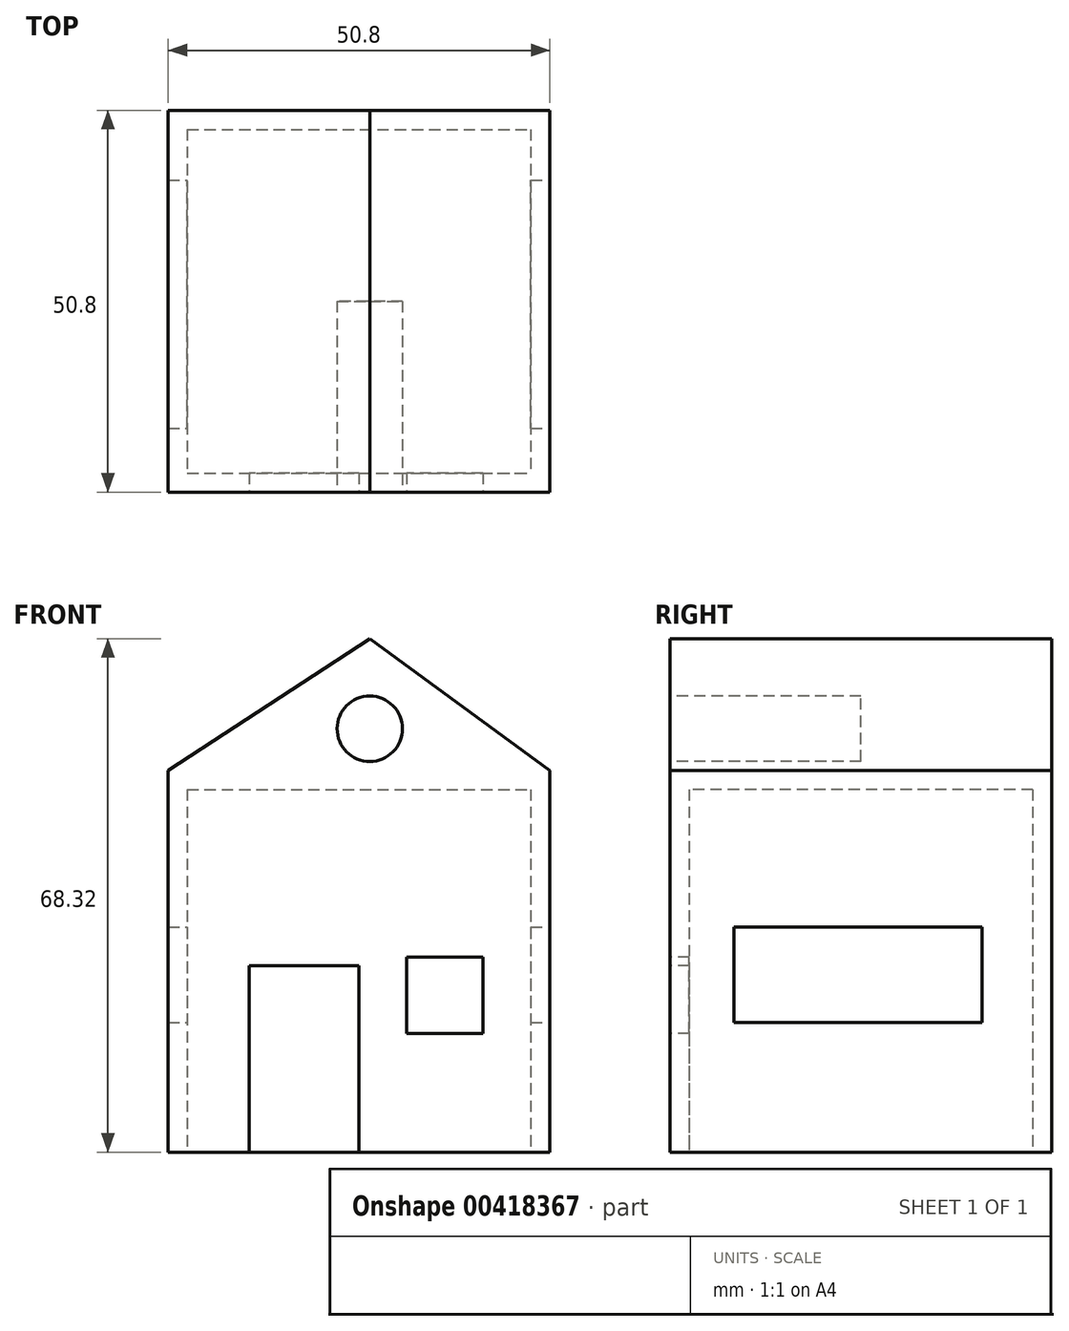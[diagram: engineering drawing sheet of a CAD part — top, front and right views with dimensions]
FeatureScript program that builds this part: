
annotation { "Feature Type Name" : "Feature", "Feature Type Description" : "" }
export const myFeature = defineFeature(function(context is Context, id is Id, definition is map)
    precondition{}
    {
        {
            var Q0;
            Q0=qCreatedBy(makeId("Top.planeOp"),FACE);
            var sketch = newSketch(context, id + "F0", { "sketchPlane" : qUnion([Q0])});
            skLineSegment(sketch, "E0.bottom", {"start": v(-26.83, 28.1) * mm, "end": v(23.97, 28.1) * mm});
            skLineSegment(sketch, "E0.top", {"start": v(-26.83, -22.7) * mm, "end": v(23.97, -22.7) * mm});
            skLineSegment(sketch, "E0.left", {"start": v(-26.83, 28.1) * mm, "end": v(-26.83, -22.7) * mm});
            skLineSegment(sketch, "E0.right", {"start": v(23.97, 28.1) * mm, "end": v(23.97, -22.7) * mm});
            skSolve(sketch);
        }
        {
            var Q0;
            Q0 = qSketchRegion(id + "F0", true);
            extrude(context, id + "F1", {"entities" : qUnion([Q0]), "depth" : 50.8 * mm});
        }
        {
            var Q0;
            Q0=makeQuery(id+"F1.opExtrude","CAP_FACE",FACE,{"disambiguationData":[OSD([sQuery(id+"F0.wireOp",EDGE,"E0.bottom"),sQuery(id+"F0.wireOp",EDGE,"E0.top"),sQuery(id+"F0.wireOp",EDGE,"E0.left"),sQuery(id+"F0.wireOp",EDGE,"E0.right")])],"isStart":true});
            shell(context, id + "F2", {"entities" : qUnion([Q0]), "thickness" : 2.54 * mm});
        }
        {
            var Q0;
            Q0=makeQuery(id+"F1.opExtrude","SWEPT_FACE",FACE,{"disambiguationData":[OSD([sQuery(id+"F0.wireOp",EDGE,"E0.top")])]});
            var sketch = newSketch(context, id + "F3", { "sketchPlane" : qUnion([Q0])});
            skLineSegment(sketch, "E1.bottom", {"start": v(-16.08, 0) * mm, "end": v(-1.43, 0) * mm});
            skLineSegment(sketch, "E1.top", {"start": v(-16.08, 24.8) * mm, "end": v(-1.43, 24.8) * mm});
            skLineSegment(sketch, "E1.left", {"start": v(-1.43, 0) * mm, "end": v(-1.43, 24.8) * mm});
            skLineSegment(sketch, "E1.right", {"start": v(-16.08, 0) * mm, "end": v(-16.08, 24.8) * mm});
            skLineSegment(sketch, "E2.bottom", {"start": v(4.9, 25.95) * mm, "end": v(15.06, 25.95) * mm});
            skLineSegment(sketch, "E2.top", {"start": v(4.9, 15.79) * mm, "end": v(15.06, 15.79) * mm});
            skLineSegment(sketch, "E2.left", {"start": v(4.9, 25.95) * mm, "end": v(4.9, 15.79) * mm});
            skLineSegment(sketch, "E2.right", {"start": v(15.06, 25.95) * mm, "end": v(15.06, 15.79) * mm});
            skSolve(sketch);
        }
        {
            var Q0;
            Q0 = qSketchRegion(id + "F3", true);
            extrude(context, id + "F4", {"entities" : qUnion([Q0]), "operationType" : NewBodyOperationType.REMOVE, "oppositeDirection" : true, "depth" : 22.35 * mm});
        }
        {
            var Q0;
            Q0=makeQuery(id+"F1.opExtrude","SWEPT_FACE",FACE,{"disambiguationData":[OSD([sQuery(id+"F0.wireOp",EDGE,"E0.top")])]});
            var sketch = newSketch(context, id + "F5", { "sketchPlane" : qUnion([Q0])});
            skLineSegment(sketch, "E3", {"start": v(-26.83, 50.8) * mm, "end": v(0, 68.32) * mm});
            skLineSegment(sketch, "E4", {"start": v(0, 68.32) * mm, "end": v(23.97, 50.8) * mm});
            skLineSegment(sketch, "E5", {"start": v(23.97, 50.8) * mm, "end": v(-26.83, 50.8) * mm});
            skSolve(sketch);
        }
        {
            var Q0;
            Q0 = qSketchRegion(id + "F5", true);
            extrude(context, id + "F6", {"entities" : qUnion([Q0]), "operationType" : NewBodyOperationType.ADD, "oppositeDirection" : true, "depth" : 50.8 * mm});
        }
        {
            var Q0;
            Q0=makeQuery(id+"F1.opExtrude","SWEPT_FACE",FACE,{"disambiguationData":[OSD([sQuery(id+"F0.wireOp",EDGE,"E0.right")])]});
            var sketch = newSketch(context, id + "F7", { "sketchPlane" : qUnion([Q0])});
            skLineSegment(sketch, "E6.bottom", {"start": v(-14.22, 29.97) * mm, "end": v(18.8, 29.97) * mm});
            skLineSegment(sketch, "E6.top", {"start": v(-14.22, 17.27) * mm, "end": v(18.8, 17.27) * mm});
            skLineSegment(sketch, "E6.left", {"start": v(-14.22, 29.97) * mm, "end": v(-14.22, 17.27) * mm});
            skLineSegment(sketch, "E6.right", {"start": v(18.8, 29.97) * mm, "end": v(18.8, 17.27) * mm});
            skSolve(sketch);
        }
        {
            var Q0;
            Q0 = qSketchRegion(id + "F7", true);
            extrude(context, id + "F8", {"entities" : qUnion([Q0]), "operationType" : NewBodyOperationType.REMOVE, "oppositeDirection" : true, "depth" : 84.84 * mm});
        }
        {
            var Q0;
            Q0=makeQuery(id+"F6.boolean.opBoolean","MERGE",FACE,{"derivedFrom":[makeQuery(id+"F1.opExtrude","SWEPT_FACE",FACE,{"disambiguationData":[OSD([sQuery(id+"F0.wireOp",EDGE,"E0.top")])]}),makeQuery(id+"F6.opExtrude","CAP_FACE",FACE,{"disambiguationData":[OSD([sQuery(id+"F5.wireOp",EDGE,"E3"),sQuery(id+"F5.wireOp",EDGE,"E4"),sQuery(id+"F5.wireOp",EDGE,"E5")])],"isStart":true})]});
            var sketch = newSketch(context, id + "F9", { "sketchPlane" : qUnion([Q0])});
            skCircle(sketch, "E7", {"center": v(0, 56.34) * mm, "radius": 4.35 * mm});
            skSolve(sketch);
        }
        {
            var Q0;
            Q0 = qSketchRegion(id + "F9", true);
            extrude(context, id + "F10", {"entities" : qUnion([Q0]), "operationType" : NewBodyOperationType.REMOVE, "oppositeDirection" : true, "depth" : 25.4 * mm});
        }
    });
